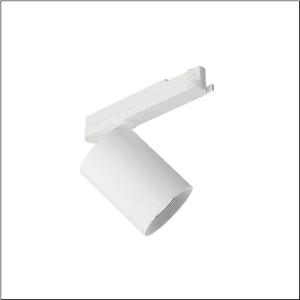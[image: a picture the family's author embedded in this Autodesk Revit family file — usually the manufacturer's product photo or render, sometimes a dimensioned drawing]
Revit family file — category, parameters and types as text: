
# Revit family: spot_21_51se13dbb5b
name_source: partatom
category: Lighting Fixtures
units: mm (PartAtom-declared; Revit-internal decimal feet)

## family parameters
Cut with Voids When Loaded = No
Host = Face
Light Source = No
Part Type = Normal
Room Calculation Point = No
Round Connector Dimension = Use Diameter
Shared = No

## types (1)
- --- (1 x LED, 5160 lm, 42.4 W, 3000K)
    Apparent Load = 42 VA
    CIE Flux Codes = 95 98 99 100 100
    Color Rendering = 90
    Color Temperature = 3000K
    Default Elevation = 1800 mm
    Description = Spot 21, directional spotlight, light control with lens, of PMMA, LED rated luminous flux: 5.120lm, light colour: 930, control gear: ECG Multilumen, with 3-phase adapter, mains connection: 220..240V, AC, 50/60Hz, of aluminium, traffic white (RAL 9016), length: 253mm, diameter: 105mm, protection rating (complete): IP20, insulation class (complete): insulation class I (protective earthing), certification: CE, impact resistance: IK02, permissible ambient temperature for indoor applications: -20..+40°C, packaging unit: 1 piece
    Height = 175 mm
    Lamp = 1 x LED
    Lamp Light Flux = 5160 lm
    Lamp Power = 42.4 W
    Lamp count = 1
    Length = 105 mm
    Luminous efficacy = 122 lm/W
    Manufacturer = Siteco
    ModVariant = No
    Model = 51SE13DBB5B
    Mounting Place = Ceiling
    Mounting Type = Pendant
    Number of Poles = 1
    OnlyDefault = Yes
    Power Factor = 1
    Product Name = Spot 21
    Product group = directional spotlight
    ProductGroupID = 905
    Protection Class = Protection class I
    Protection Degree = IP 20
    RLX_Detail_Level = 1
    RLX_Emergency_Light_Flux = 0 lm
    RLX_Emergency_Type = 0
    RLX_Emergency_Type_DB = No
    RlxData = <blob elided: 17661 chars, md5=52343502>
    Socket = socket
    Standby Power = 0 W
    System Light Flux = 5160 lm
    System Power = 42 W
    Type Comments = factory setting: luminous flux: 100 % | (ON | ON | ON | ON) | 1050 mA
    Type Image = l_1003976.jpg
    URL = http://relux.com
    VarID = @adj_114051
    Voltage = 0 V
    Weight = 0.00 kg
    Width = 0 mm  [stored 0 ft]

note: [stored X ft] marks values corroborated as IEEE doubles in the binary element streams (Revit-internal decimal feet)

## geometry (parser evidence)
native form markers: Blend x4, Sweep x11
no freeform markers — native parametric forms only
